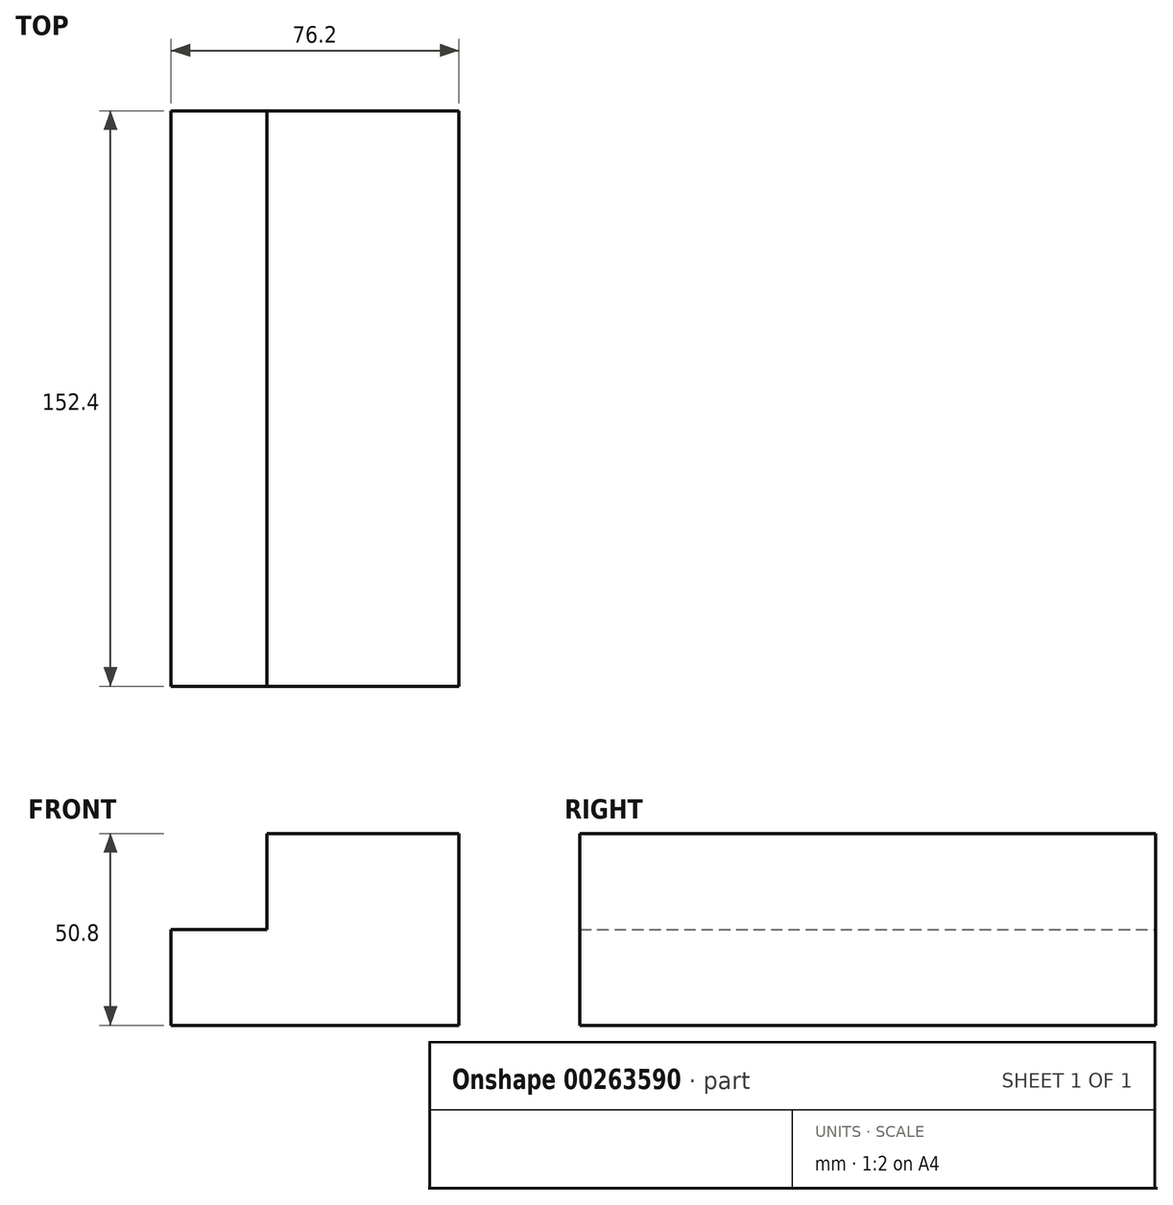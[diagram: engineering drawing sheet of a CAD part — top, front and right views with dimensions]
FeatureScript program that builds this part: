
annotation { "Feature Type Name" : "Feature", "Feature Type Description" : "" }
export const myFeature = defineFeature(function(context is Context, id is Id, definition is map)
    precondition{}
    {
        {
            var Q0;
            Q0=qCreatedBy(makeId("Front.planeOp"),FACE);
            var sketch = newSketch(context, id + "F0", { "sketchPlane" : qUnion([Q0])});
            skLineSegment(sketch, "E0", {"start": v(-37.9, 0) * mm, "end": v(38.3, 0) * mm});
            skLineSegment(sketch, "E1", {"start": v(38.3, 0) * mm, "end": v(38.3, 50.8) * mm});
            skLineSegment(sketch, "E2", {"start": v(-37.9, 0) * mm, "end": v(-37.9, 25.4) * mm});
            skLineSegment(sketch, "E3", {"start": v(-37.9, 25.4) * mm, "end": v(-12.5, 25.4) * mm});
            skLineSegment(sketch, "E4", {"start": v(-12.5, 25.4) * mm, "end": v(-12.5, 50.8) * mm});
            skLineSegment(sketch, "E5", {"start": v(38.3, 50.8) * mm, "end": v(-12.5, 50.8) * mm});
            skSolve(sketch);
        }
        {
            var Q0;
            Q0=makeQuery(id+"F0.imprint","IMPRINT",FACE,{"disambiguationData":[TD([[makeQuery(id+"F0.imprint","IMPRINT",EDGE,{"derivedFrom":sQuery(id+"F0.wireOp",EDGE,"E0")}),1.0]])]});
            extrude(context, id + "F1", {"entities" : qUnion([Q0]), "depth" : 152.4 * mm});
        }
    });
